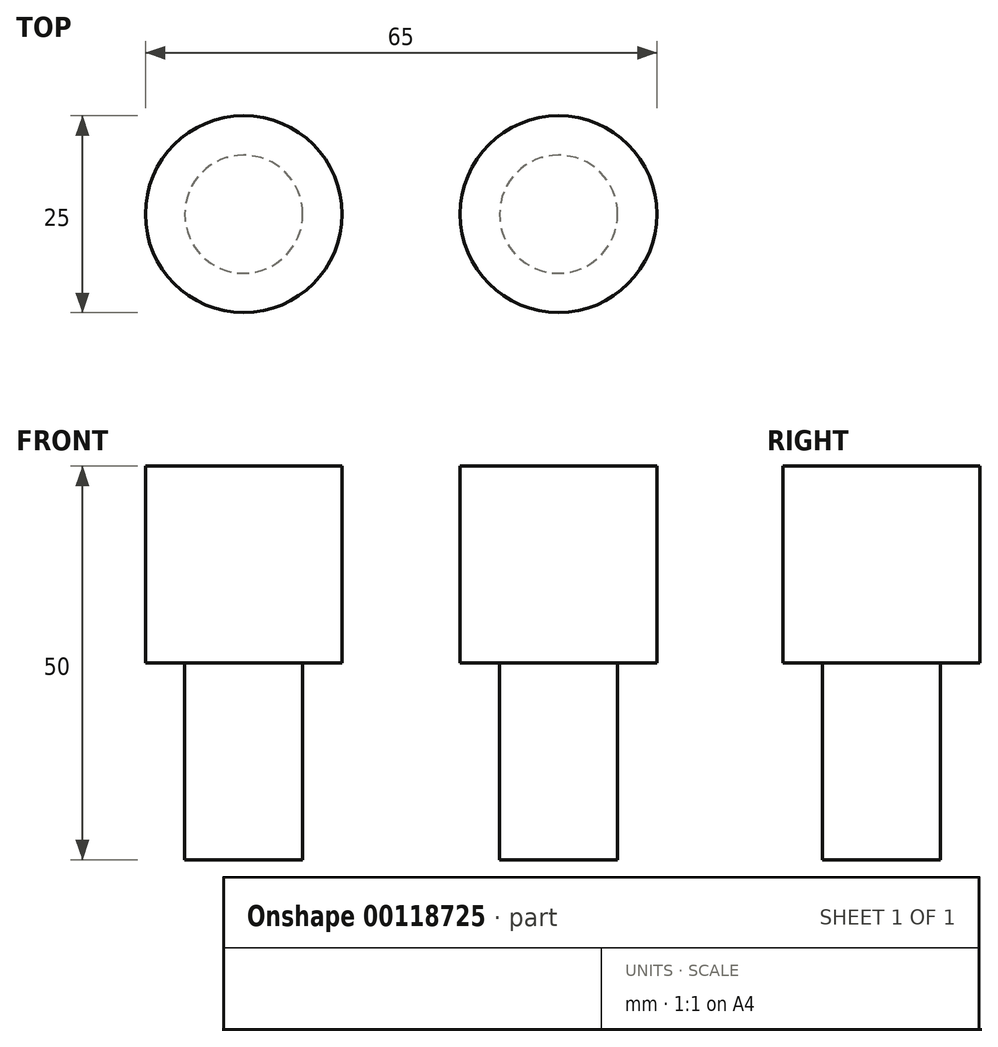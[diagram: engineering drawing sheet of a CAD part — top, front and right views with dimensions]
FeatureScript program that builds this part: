
annotation { "Feature Type Name" : "Feature", "Feature Type Description" : "" }
export const myFeature = defineFeature(function(context is Context, id is Id, definition is map)
    precondition{}
    {
        {
            var Q0;
            Q0=qCreatedBy(makeId("Top.planeOp"),FACE);
            var sketch = newSketch(context, id + "F0", { "sketchPlane" : qUnion([Q0])});
            skCircle(sketch, "E0", {"center": v(-20, 0) * mm, "radius": 7.5 * mm});
            skCircle(sketch, "E1", {"center": v(20, 0) * mm, "radius": 7.5 * mm});
            skSolve(sketch);
        }
        {
            var Q0;
            Q0=makeQuery(id+"F0.imprint","IMPRINT",FACE,{"disambiguationData":[TD([[makeQuery(id+"F0.imprint","IMPRINT",EDGE,{"derivedFrom":sQuery(id+"F0.wireOp",EDGE,"E0")}),1.0]])]});
            var Q1;
            Q1=makeQuery(id+"F0.imprint","IMPRINT",FACE,{"disambiguationData":[TD([[makeQuery(id+"F0.imprint","IMPRINT",EDGE,{"derivedFrom":sQuery(id+"F0.wireOp",EDGE,"E1")}),1.0]])]});
            extrude(context, id + "F1", {"entities" : qUnion([Q0, Q1]), "depth" : 25 * mm});
        }
        {
            var Q0;
            Q0=makeQuery(id+"F1.opExtrude","CAP_FACE",FACE,{"disambiguationData":[OSD([sQuery(id+"F0.wireOp",EDGE,"E0")])],"isStart":false});
            var Q1;
            Q1=makeQuery(id+"F1.opExtrude","CAP_FACE",FACE,{"disambiguationData":[OSD([sQuery(id+"F0.wireOp",EDGE,"E1")])],"isStart":false});
            cPlane(context, id + "F2", {"entities" : qUnion([Q0, Q1]), "cplaneType" : CPlaneType.MID_PLANE, "offset" : 25 * mm, "width" : 150 * mm, "height" : 150 * mm});
        }
        {
            var Q0;
            Q0=qCreatedBy(id+"F2.planeOp",FACE);
            var sketch = newSketch(context, id + "F3", { "sketchPlane" : qUnion([Q0])});
            skCircle(sketch, "E2.0", {"center": v(-20, 0) * mm, "radius": 12.5 * mm});
            skCircle(sketch, "E3.0", {"center": v(20, 0) * mm, "radius": 12.5 * mm});
            skSolve(sketch);
        }
        {
            var Q0;
            Q0=makeQuery(id+"F3.imprint","IMPRINT",FACE,{"disambiguationData":[TD([[makeQuery(id+"F3.imprint","IMPRINT",EDGE,{"derivedFrom":sQuery(id+"F3.wireOp",EDGE,"E2.0")}),1.0]])]});
            var Q1;
            Q1=makeQuery(id+"F3.imprint","IMPRINT",FACE,{"disambiguationData":[TD([[makeQuery(id+"F3.imprint","IMPRINT",EDGE,{"derivedFrom":sQuery(id+"F3.wireOp",EDGE,"E3.0")}),1.0]])]});
            extrude(context, id + "F4", {"entities" : qUnion([Q0, Q1]), "depth" : 25 * mm});
        }
    });
